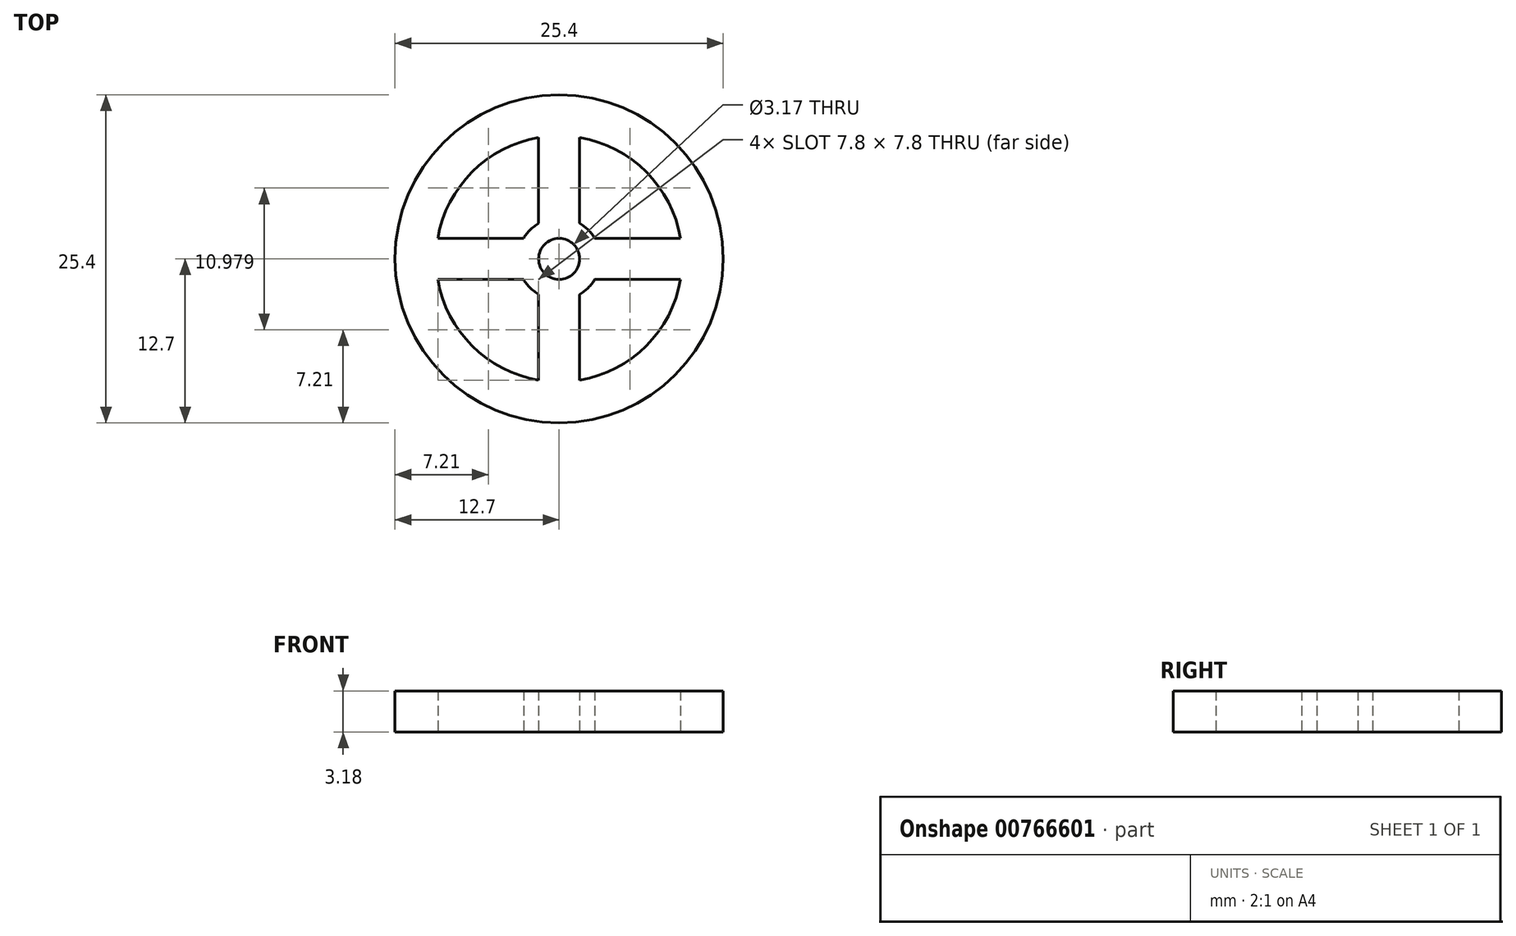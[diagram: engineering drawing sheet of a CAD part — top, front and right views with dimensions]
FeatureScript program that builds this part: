
annotation { "Feature Type Name" : "Feature", "Feature Type Description" : "" }
export const myFeature = defineFeature(function(context is Context, id is Id, definition is map)
    precondition{}
    {
        {
            var Q0;
            Q0=qCreatedBy(makeId("Top.planeOp"),FACE);
            var sketch = newSketch(context, id + "F0", { "sketchPlane" : qUnion([Q0])});
            skCircle(sketch, "E0", {"center": v(0, 0) * mm, "radius": 12.7 * mm});
            skArc(sketch, "E1", {"start": v(-9.4, -1.59) * mm, "mid": v(-6.74, -6.74) * mm, "end": v(-1.59, -9.4) * mm});
            skArc(sketch, "E2", {"start": v(-2.75, -1.59) * mm, "mid": v(-2.25, -2.25) * mm, "end": v(-1.59, -2.75) * mm});
            skCircle(sketch, "E3", {"center": v(0, 0) * mm, "radius": 1.59 * mm});
            skLineSegment(sketch, "E4", {"start": v(0, 0) * mm, "end": v(0, 12.7) * mm, "construction": true});
            skLineSegment(sketch, "E5", {"start": v(0, 0) * mm, "end": v(-12.7, 0) * mm, "construction": true});
            skLineSegment(sketch, "E6", {"start": v(0, 0) * mm, "end": v(0, -12.7) * mm, "construction": true});
            skLineSegment(sketch, "E7.0", {"start": v(1.59, 2.75) * mm, "end": v(1.59, 9.4) * mm});
            skLineSegment(sketch, "E8.0", {"start": v(-1.59, 2.75) * mm, "end": v(-1.59, 9.4) * mm});
            skLineSegment(sketch, "E9.0", {"start": v(-1.59, -2.75) * mm, "end": v(-1.59, -9.4) * mm});
            skLineSegment(sketch, "E10.0", {"start": v(1.59, -2.75) * mm, "end": v(1.59, -9.4) * mm});
            skLineSegment(sketch, "E11.0", {"start": v(-2.75, 1.59) * mm, "end": v(-9.4, 1.59) * mm});
            skLineSegment(sketch, "E12.0", {"start": v(-2.75, -1.59) * mm, "end": v(-9.4, -1.59) * mm});
            skLineSegment(sketch, "E13", {"start": v(0, 0) * mm, "end": v(12.7, 0) * mm, "construction": true});
            skLineSegment(sketch, "E14.0", {"start": v(2.75, -1.59) * mm, "end": v(9.4, -1.59) * mm});
            skLineSegment(sketch, "E15.0", {"start": v(2.75, 1.59) * mm, "end": v(9.4, 1.59) * mm});
            skArc(sketch, "E16.trimOffspring", {"start": v(1.59, -2.75) * mm, "mid": v(2.25, -2.25) * mm, "end": v(2.75, -1.59) * mm});
            skArc(sketch, "E17.trimOffspring", {"start": v(2.75, 1.59) * mm, "mid": v(2.25, 2.25) * mm, "end": v(1.59, 2.75) * mm});
            skArc(sketch, "E18.trimOffspring", {"start": v(-1.59, 2.75) * mm, "mid": v(-2.25, 2.25) * mm, "end": v(-2.75, 1.59) * mm});
            skArc(sketch, "E19.trimOffspring", {"start": v(9.4, 1.59) * mm, "mid": v(6.74, 6.74) * mm, "end": v(1.59, 9.4) * mm});
            skArc(sketch, "E20.trimOffspring", {"start": v(-1.59, 9.4) * mm, "mid": v(-6.74, 6.74) * mm, "end": v(-9.4, 1.59) * mm});
            skArc(sketch, "E21.trimOffspring", {"start": v(1.59, -9.4) * mm, "mid": v(6.74, -6.74) * mm, "end": v(9.4, -1.59) * mm});
            skSolve(sketch);
        }
        {
            var Q0;
            Q0=makeQuery(id+"F0.imprint","IMPRINT",FACE,{"disambiguationData":[TD([[makeQuery(id+"F0.imprint","IMPRINT",EDGE,{"derivedFrom":sQuery(id+"F0.wireOp",EDGE,"E0")}),1.0]])]});
            extrude(context, id + "F1", {"entities" : qUnion([Q0]), "depth" : 3.17 * mm, "offsetDistance" : 25.4 * mm});
        }
    });
